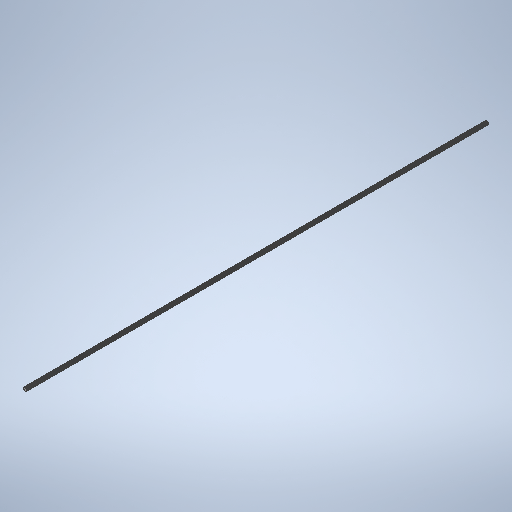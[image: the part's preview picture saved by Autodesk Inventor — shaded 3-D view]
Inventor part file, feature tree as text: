
AUTODESK INVENTOR PART (.ipt)
format: ipt  version: 2025.2 (Build 292293000, 293)  size: 3,615,232 bytes
history: native  units: mm
features: extrude x1, chamfer x1, other x1, pattern_circular x1
ambient origin geometry x8: Origin, YZ Plane, XZ Plane, XY Plane, X Axis, Y Axis, Z Axis, Center Point
bodies: Solid1 (feature_tree)
feature tree (4):
  extrude  "1000mm Rod"  Depth=1000.0mm TaperAngle=0.0deg
  chamfer  "Chamfer1"  Distance=0.907143mm Angle=45.0deg
  other  "ACME Thread 2mm Pitch"
  pattern_circular  "4 Start"  [2 undecoded]
note: 2 required parameter values undecoded (feature->parameter linkage not recoverable at this tier; creation-order binding heuristic only, values carry confidence <= 0.55)
